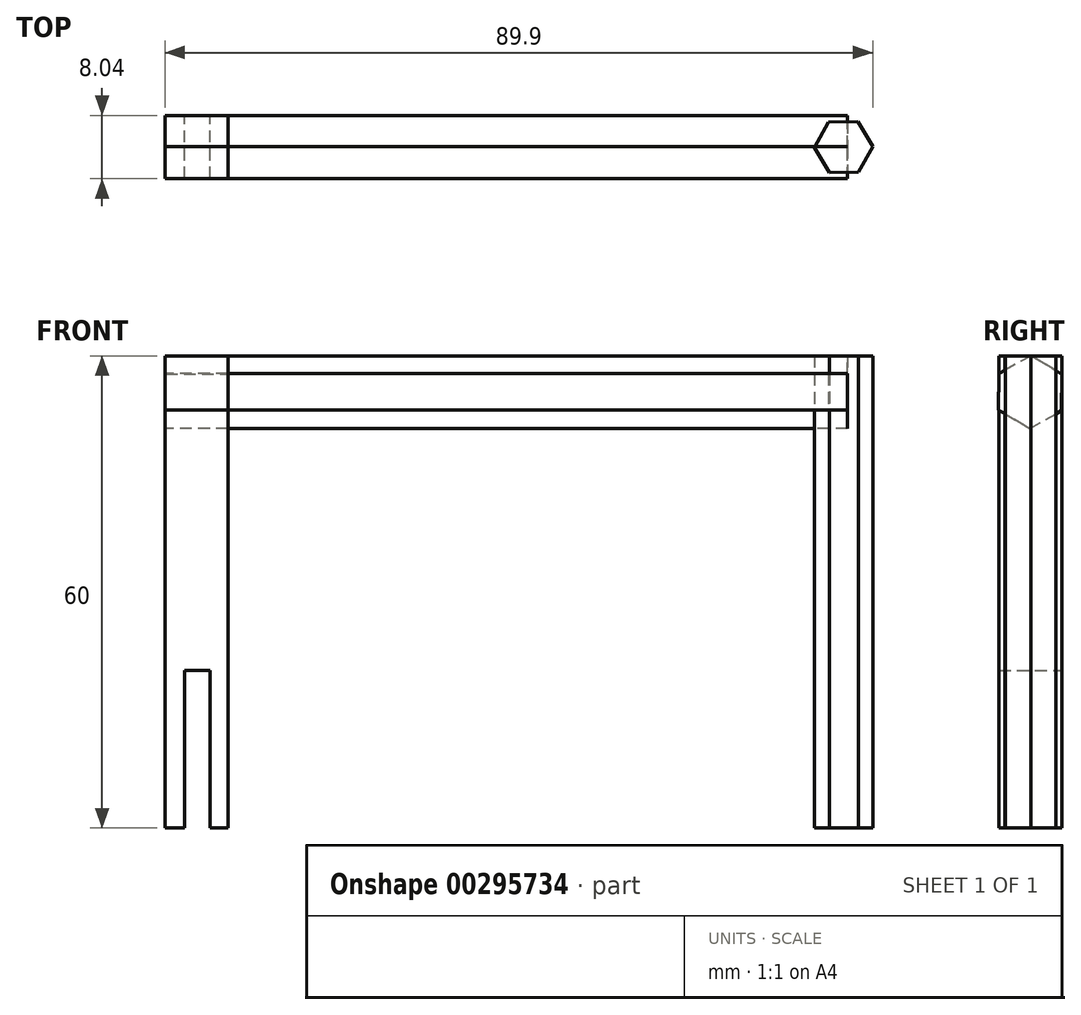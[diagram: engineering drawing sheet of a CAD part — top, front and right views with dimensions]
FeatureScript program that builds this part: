
annotation { "Feature Type Name" : "Feature", "Feature Type Description" : "" }
export const myFeature = defineFeature(function(context is Context, id is Id, definition is map)
    precondition{}
    {
        {
            var Q0;
            Q0=qCreatedBy(makeId("Front.planeOp"),FACE);
            var sketch = newSketch(context, id + "F0", { "sketchPlane" : qUnion([Q0])});
            skLineSegment(sketch, "E0", {"start": v(0, 0) * mm, "end": v(0, 60) * mm});
            skLineSegment(sketch, "E1", {"start": v(0, 60) * mm, "end": v(8, 60) * mm});
            skLineSegment(sketch, "E2", {"start": v(8, 60) * mm, "end": v(8, 0) * mm});
            skLineSegment(sketch, "E3", {"start": v(8, 0) * mm, "end": v(5.7, 0) * mm});
            skLineSegment(sketch, "E4", {"start": v(5.7, 0) * mm, "end": v(5.7, 20) * mm});
            skLineSegment(sketch, "E5", {"start": v(5.7, 20) * mm, "end": v(2.5, 20) * mm});
            skLineSegment(sketch, "E6", {"start": v(2.5, 20) * mm, "end": v(2.5, 0) * mm});
            skLineSegment(sketch, "E7", {"start": v(2.5, 0) * mm, "end": v(0, 0) * mm});
            skSolve(sketch);
        }
        {
            var Q0;
            Q0=makeQuery(id+"F0.imprint","IMPRINT",FACE,{"disambiguationData":[TD([[makeQuery(id+"F0.imprint","IMPRINT",EDGE,{"derivedFrom":sQuery(id+"F0.wireOp",EDGE,"E0")}),-1.0]])]});
            extrude(context, id + "F1", {"entities" : qUnion([Q0]), "depth" : 8 * mm});
        }
        {
            var Q0;
            Q0=qCreatedBy(makeId("Top.planeOp"),FACE);
            var sketch = newSketch(context, id + "F2", { "sketchPlane" : qUnion([Q0])});
            skCircle(sketch, "E8.cCircle", {"center": v(86.2, -4) * mm, "radius": 3.7 * mm, "construction": true});
            skLineSegment(sketch, "E8.0", {"start": v(84.3, -0.83) * mm, "end": v(88, -0.76) * mm});
            skLineSegment(sketch, "E8.1", {"start": v(88, -0.76) * mm, "end": v(89.9, -3.93) * mm});
            skLineSegment(sketch, "E8.2", {"start": v(89.9, -3.93) * mm, "end": v(88.1, -7.17) * mm});
            skLineSegment(sketch, "E8.3", {"start": v(88.1, -7.17) * mm, "end": v(84.4, -7.24) * mm});
            skLineSegment(sketch, "E8.4", {"start": v(84.4, -7.24) * mm, "end": v(82.5, -4.07) * mm});
            skLineSegment(sketch, "E8.5", {"start": v(82.5, -4.07) * mm, "end": v(84.3, -0.83) * mm});
            skSolve(sketch);
        }
        {
            var Q0;
            Q0 = qSketchRegion(id + "F2", true);
            extrude(context, id + "F3", {"entities" : qUnion([Q0]), "depth" : 60 * mm});
        }
        {
            var Q0;
            Q0=makeQuery(id+"F1.opExtrude","SWEPT_FACE",FACE,{"disambiguationData":[OSD([sQuery(id+"F0.wireOp",EDGE,"E0")])]});
            var sketch = newSketch(context, id + "F4", { "sketchPlane" : qUnion([Q0])});
            skCircle(sketch, "E9.cCircle", {"center": v(4, 55.38) * mm, "radius": 4 * mm, "construction": true});
            skLineSegment(sketch, "E9.0", {"start": v(8.02, 53.11) * mm, "end": v(4.05, 50.76) * mm});
            skLineSegment(sketch, "E9.1", {"start": v(4.05, 50.76) * mm, "end": v(0.02, 53.03) * mm});
            skLineSegment(sketch, "E9.2", {"start": v(0.02, 53.03) * mm, "end": v(-0.02, 57.65) * mm});
            skLineSegment(sketch, "E9.3", {"start": v(-0.02, 57.65) * mm, "end": v(3.95, 60) * mm});
            skLineSegment(sketch, "E9.4", {"start": v(3.95, 60) * mm, "end": v(7.98, 57.73) * mm});
            skLineSegment(sketch, "E9.5", {"start": v(7.98, 57.73) * mm, "end": v(8.02, 53.11) * mm});
            skPoint(sketch, "E9.0.midPoint", {"position": v(6.04, 51.94) * mm});
            skSolve(sketch);
        }
        {
            var Q0;
            Q0 = qSketchRegion(id + "F4", true);
            var Q1;
            {var subQ1=sQuery(id+"F4.wireOp",EDGE,"E9.1");Q1=makeQuery(id+"F4.imprint","IMPRINT",FACE,{"disambiguationData":[TD([[makeQuery(id+"F4.imprint","IMPRINT",EDGE,{"derivedFrom":subQ1}),-1.0]])]});}
            extrude(context, id + "F5", {"entities" : qUnion([Q0, Q1]), "oppositeDirection" : true, "depth" : 86.7 * mm});
        }
    });
